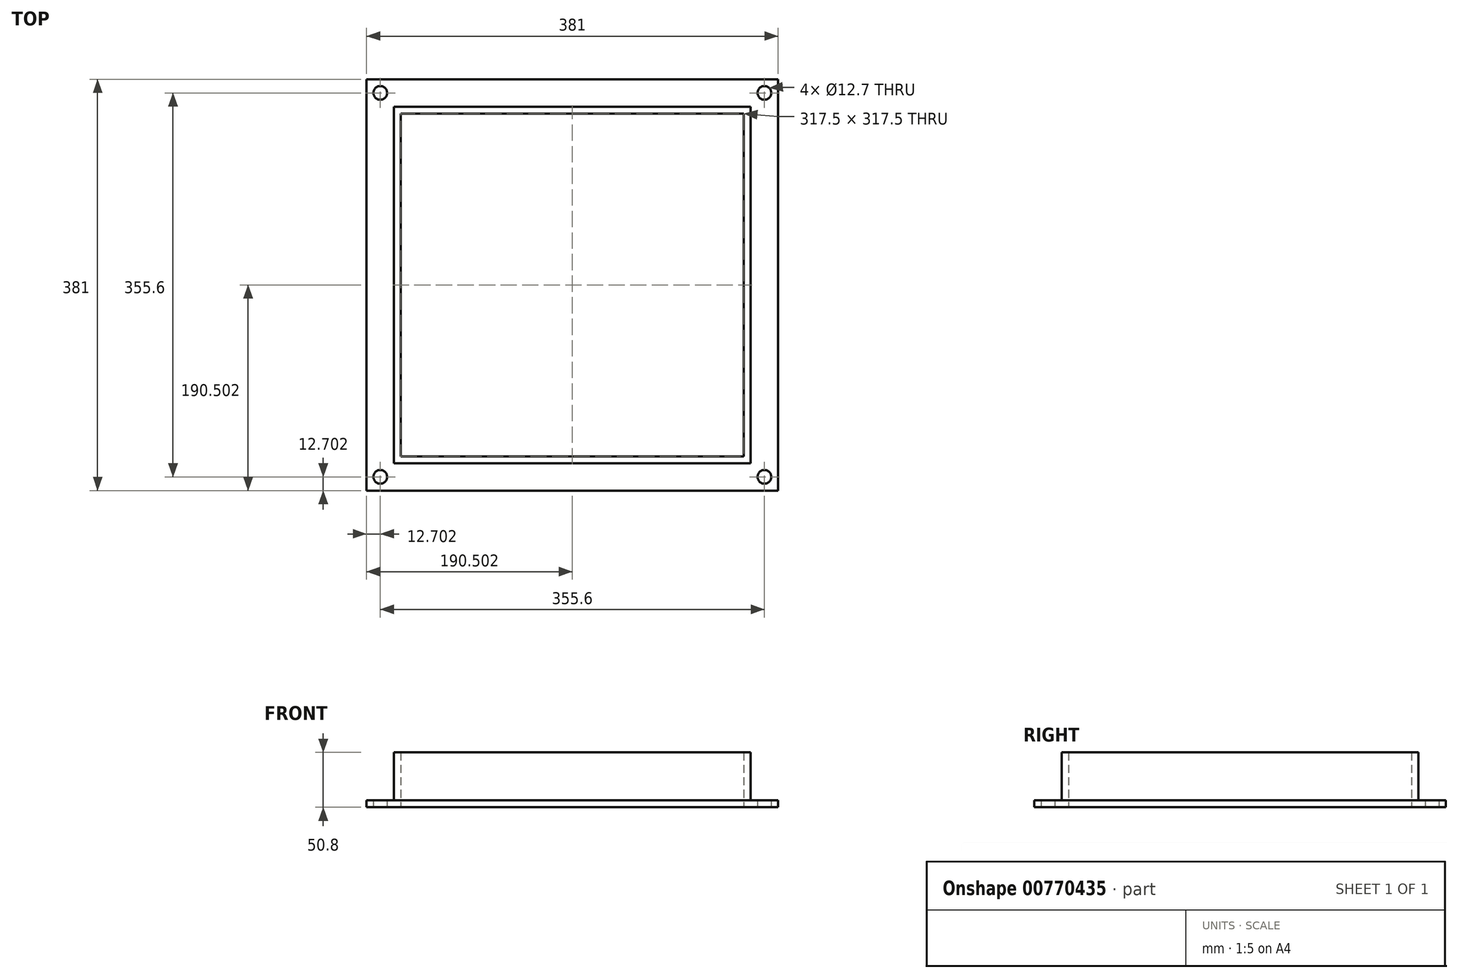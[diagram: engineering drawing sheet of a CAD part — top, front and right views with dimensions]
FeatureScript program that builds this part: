
annotation { "Feature Type Name" : "Feature", "Feature Type Description" : "" }
export const myFeature = defineFeature(function(context is Context, id is Id, definition is map)
    precondition{}
    {
        {
            var Q0;
            Q0=qCreatedBy(makeId("Top.planeOp"),FACE);
            var sketch = newSketch(context, id + "F0", { "sketchPlane" : qUnion([Q0])});
            skLineSegment(sketch, "E0.bottom", {"start": v(-174.97, 186.05) * mm, "end": v(206.03, 186.05) * mm});
            skLineSegment(sketch, "E0.top", {"start": v(-174.97, -194.95) * mm, "end": v(206.03, -194.95) * mm});
            skLineSegment(sketch, "E0.left", {"start": v(-174.97, 186.05) * mm, "end": v(-174.97, -194.95) * mm});
            skLineSegment(sketch, "E0.right", {"start": v(206.03, 186.05) * mm, "end": v(206.03, -194.95) * mm});
            skLineSegment(sketch, "E1.bottom", {"start": v(-149.57, 160.65) * mm, "end": v(180.63, 160.65) * mm});
            skLineSegment(sketch, "E1.top", {"start": v(-149.57, -169.55) * mm, "end": v(180.63, -169.55) * mm});
            skLineSegment(sketch, "E1.left", {"start": v(-149.57, 160.65) * mm, "end": v(-149.57, -169.55) * mm});
            skLineSegment(sketch, "E1.right", {"start": v(180.63, 160.65) * mm, "end": v(180.63, -169.55) * mm});
            skLineSegment(sketch, "E2.bottom", {"start": v(-143.22, 154.3) * mm, "end": v(174.28, 154.3) * mm});
            skLineSegment(sketch, "E2.top", {"start": v(-143.22, -163.2) * mm, "end": v(174.28, -163.2) * mm});
            skLineSegment(sketch, "E2.left", {"start": v(-143.22, 154.3) * mm, "end": v(-143.22, -163.2) * mm});
            skLineSegment(sketch, "E2.right", {"start": v(174.28, 154.3) * mm, "end": v(174.28, -163.2) * mm});
            skCircle(sketch, "E3", {"center": v(-162.27, 173.35) * mm, "radius": 6.35 * mm});
            skCircle(sketch, "E4", {"center": v(-162.27, -182.25) * mm, "radius": 6.35 * mm});
            skCircle(sketch, "E5", {"center": v(193.33, -182.25) * mm, "radius": 6.35 * mm});
            skCircle(sketch, "E6", {"center": v(193.33, 173.35) * mm, "radius": 6.35 * mm});
            skSolve(sketch);
        }
        {
            var Q0;
            Q0 = qSketchRegion(id + "F0", true);
            extrude(context, id + "F1", {"entities" : qUnion([Q0]), "depth" : 6.35 * mm, "offsetDistance" : 25.4 * mm});
        }
        {
            var Q0;
            Q0=makeQuery(id+"F0.imprint","IMPRINT",FACE,{"disambiguationData":[TD([[makeQuery(id+"F0.imprint","IMPRINT",EDGE,{"derivedFrom":sQuery(id+"F0.wireOp",EDGE,"E1.bottom")}),-1.0]])]});
            extrude(context, id + "F2", {"entities" : qUnion([Q0]), "operationType" : NewBodyOperationType.ADD, "depth" : 50.8 * mm, "offsetDistance" : 25.4 * mm});
        }
    });
